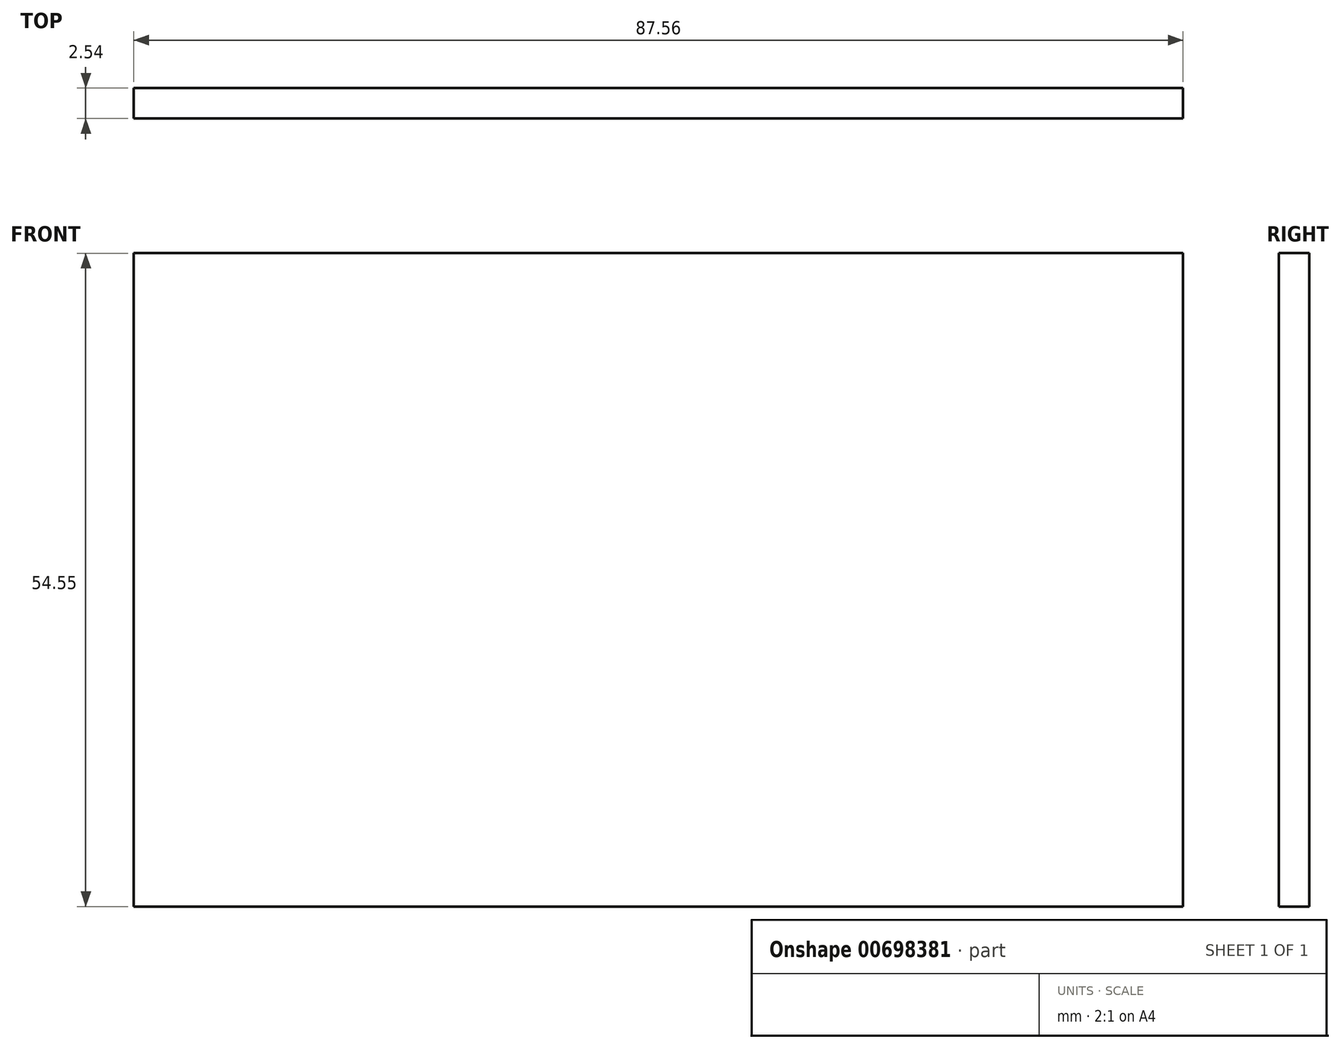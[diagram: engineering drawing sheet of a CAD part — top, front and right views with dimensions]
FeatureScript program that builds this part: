
annotation { "Feature Type Name" : "Feature", "Feature Type Description" : "" }
export const myFeature = defineFeature(function(context is Context, id is Id, definition is map)
    precondition{}
    {
        {
            var Q0;
            Q0=qCreatedBy(makeId("Front.planeOp"),FACE);
            var sketch = newSketch(context, id + "F0", { "sketchPlane" : qUnion([Q0])});
            skLineSegment(sketch, "E0.bottom", {"start": v(-44.34, -22.8) * mm, "end": v(43.22, -22.8) * mm});
            skLineSegment(sketch, "E0.top", {"start": v(-44.34, 31.75) * mm, "end": v(43.22, 31.75) * mm});
            skLineSegment(sketch, "E0.left", {"start": v(-44.34, -22.8) * mm, "end": v(-44.34, 31.75) * mm});
            skLineSegment(sketch, "E0.right", {"start": v(43.22, -22.8) * mm, "end": v(43.22, 31.75) * mm});
            skSolve(sketch);
        }
        {
            var Q0;
            Q0=makeQuery(id+"F0.imprint","IMPRINT",FACE,{"disambiguationData":[TD([[makeQuery(id+"F0.imprint","IMPRINT",EDGE,{"derivedFrom":sQuery(id+"F0.wireOp",EDGE,"E0.bottom")}),1.0]])]});
            extrude(context, id + "F1", {"entities" : qUnion([Q0]), "depth" : 2.54 * mm, "offsetDistance" : 25.4 * mm});
        }
    });
